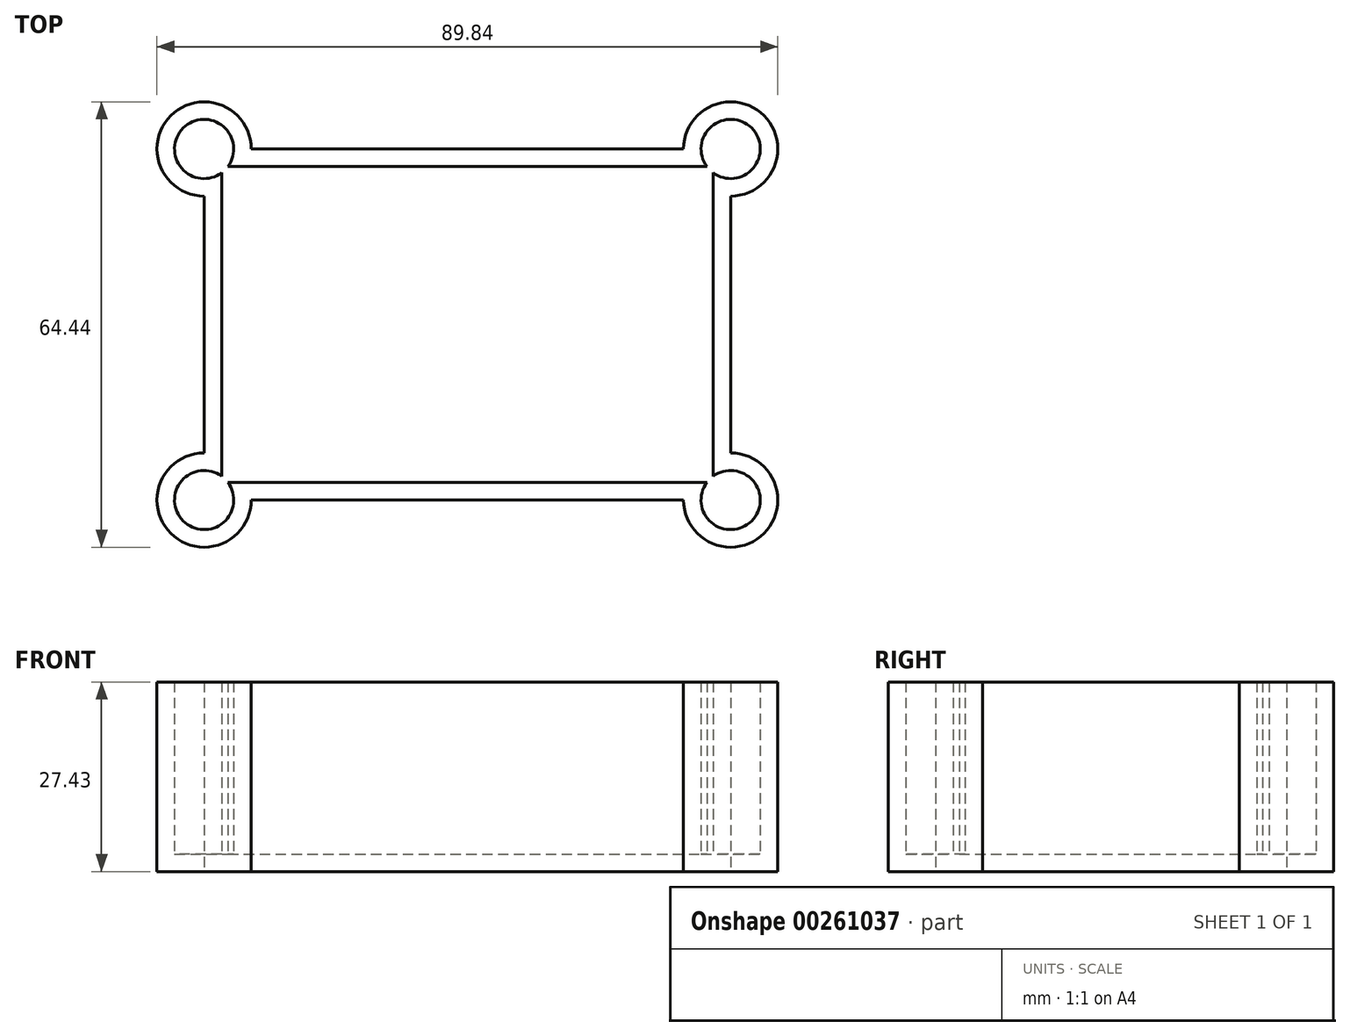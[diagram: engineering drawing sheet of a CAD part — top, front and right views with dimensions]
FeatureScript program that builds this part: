
annotation { "Feature Type Name" : "Feature", "Feature Type Description" : "" }
export const myFeature = defineFeature(function(context is Context, id is Id, definition is map)
    precondition{}
    {
        {
            var Q0;
            Q0=qCreatedBy(makeId("Top.planeOp"),FACE);
            var sketch = newSketch(context, id + "F0", { "sketchPlane" : qUnion([Q0])});
            skPoint(sketch, "E0.middle", {"position": v(0, 0) * mm});
            skLineSegment(sketch, "E1.bottom", {"start": v(-38.1, -25.4) * mm, "end": v(38.1, -25.4) * mm});
            skLineSegment(sketch, "E1.top", {"start": v(-38.1, 25.4) * mm, "end": v(38.1, 25.4) * mm});
            skLineSegment(sketch, "E1.left", {"start": v(-38.1, -25.4) * mm, "end": v(-38.1, 25.4) * mm});
            skLineSegment(sketch, "E1.right", {"start": v(38.1, -25.4) * mm, "end": v(38.1, 25.4) * mm});
            skCircle(sketch, "E2", {"center": v(-38.1, 25.4) * mm, "radius": 6.82 * mm});
            skCircle(sketch, "E3", {"center": v(38.1, 25.4) * mm, "radius": 6.82 * mm});
            skCircle(sketch, "E4", {"center": v(38.1, -25.4) * mm, "radius": 6.82 * mm});
            skCircle(sketch, "E5", {"center": v(-38.1, -25.4) * mm, "radius": 6.82 * mm});
            skSolve(sketch);
        }
        {
            var Q0;
            Q0 = qSketchRegion(id + "F0", true);
            extrude(context, id + "F1", {"entities" : qUnion([Q0]), "depth" : 27.43 * mm});
        }
        {
            var Q0;
            Q0=makeQuery(id+"F1.opExtrude","CAP_FACE",FACE,{"disambiguationData":[OSD([sQuery(id+"F0.wireOp",EDGE,"E1.bottom"),sQuery(id+"F0.wireOp",EDGE,"E1.top"),sQuery(id+"F0.wireOp",EDGE,"E1.left"),sQuery(id+"F0.wireOp",EDGE,"E1.right")])],"isStart":false});
            shell(context, id + "F2", {"entities" : qUnion([Q0]), "thickness" : 2.54 * mm});
        }
        {
            var Q0;
            Q0=qCreatedBy(makeId("Top.planeOp"),FACE);
            var sketch = newSketch(context, id + "F3", { "sketchPlane" : qUnion([Q0])});
            skArc(sketch, "E6", {"start": v(-36.45, 12.95) * mm, "mid": v(-42.32, -1.55) * mm, "end": v(-36.04, -15.88) * mm});
            skArc(sketch, "E7", {"start": v(36.45, -14.83) * mm, "mid": v(43.5, -1.35) * mm, "end": v(36.04, 11.9) * mm});
            skArc(sketch, "E8", {"start": v(-36.25, 9.31) * mm, "mid": v(-39.85, -2.1) * mm, "end": v(-35.88, -13.4) * mm});
            skArc(sketch, "E9", {"start": v(35.77, -12.09) * mm, "mid": v(40.97, -1.85) * mm, "end": v(35.77, 8.38) * mm});
            skSolve(sketch);
        }
        {
            var Q0;
            Q0=sQuery(id+"F3.wireOp",EDGE,"E6");
            var Q1;
            Q1=sQuery(id+"F3.wireOp",EDGE,"E8");
            var Q2;
            Q2=sQuery(id+"F3.wireOp",EDGE,"E9");
            var Q3;
            Q3=sQuery(id+"F3.wireOp",EDGE,"E7");
            extrude(context, id + "F4", {"bodyType" : ToolBodyType.SURFACE, "surfaceEntities" : qUnion([Q0, Q1, Q2, Q3]), "depth" : 18.54 * mm});
        }
    });
